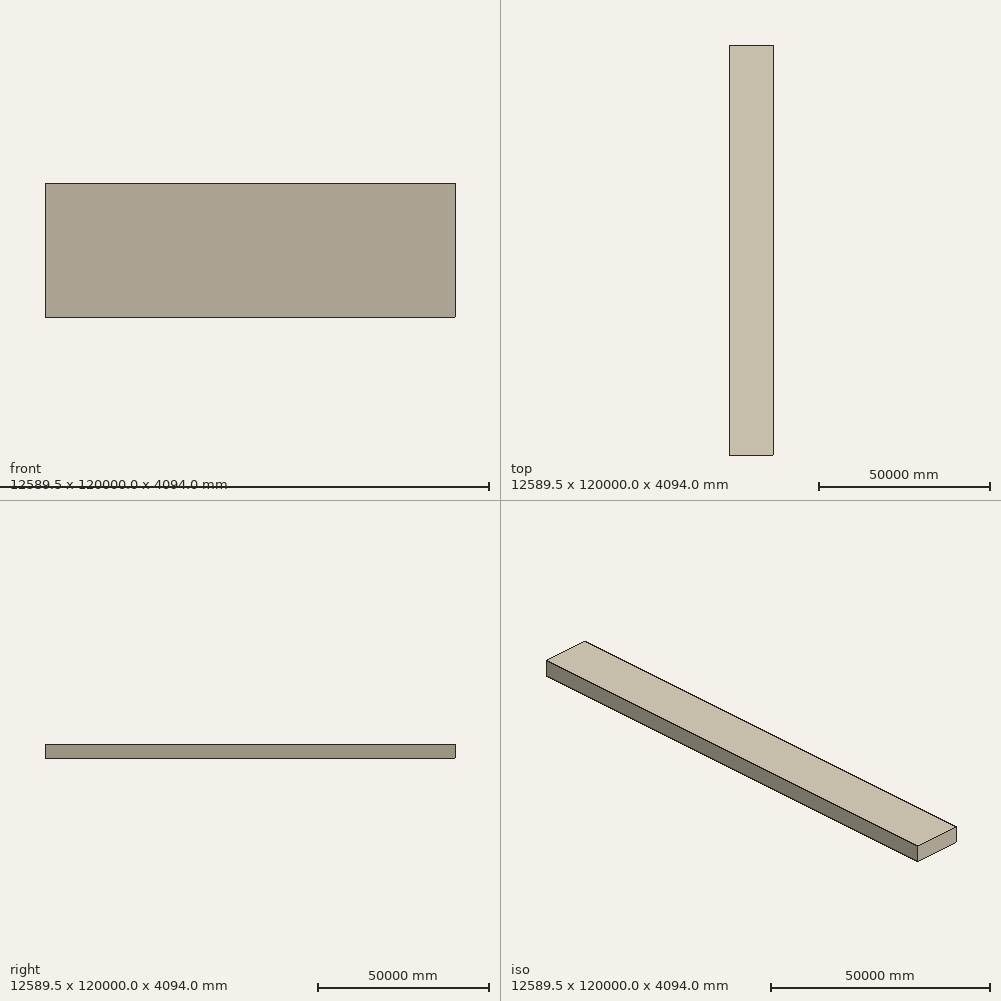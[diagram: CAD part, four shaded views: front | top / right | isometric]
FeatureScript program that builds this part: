
annotation { "Feature Type Name" : "Feature", "Feature Type Description" : "" }
export const myFeature = defineFeature(function(context is Context, id is Id, definition is map)
    precondition{}
    {
        {
            var Q0;
            Q0=qCreatedBy(makeId("Front.planeOp"),FACE);
            var sketch = newSketch(context, id + "F0", { "sketchPlane" : qUnion([Q0])});
            skLineSegment(sketch, "E0", {"start": v(0, 0) * mm, "end": v(12589.52, 0) * mm});
            skSolve(sketch);
        }
        {
            var Q0;
            Q0 = qSketchRegion(id + "F0", true);
            var Q1;
            Q1=sQuery(id+"F0.wireOp",EDGE,"E0");
            extrude(context, id + "F1", {"entities" : qUnion([Q0]), "bodyType" : ToolBodyType.SURFACE, "surfaceEntities" : qUnion([Q1]), "depth" : 120000 * mm, "offsetDistance" : 25 * mm});
        }
        {
            var Q0;
            Q0=makeQuery(id+"F1.opExtrude","SWEPT_FACE",FACE,{"disambiguationData":[OSD([sQuery(id+"F0.wireOp",EDGE,"E0")])]});
            extrude(context, id + "F2", {"entities" : qUnion([Q0]), "oppositeDirection" : true, "depth" : 4094 * mm, "offsetDistance" : 25 * mm});
        }
    });
